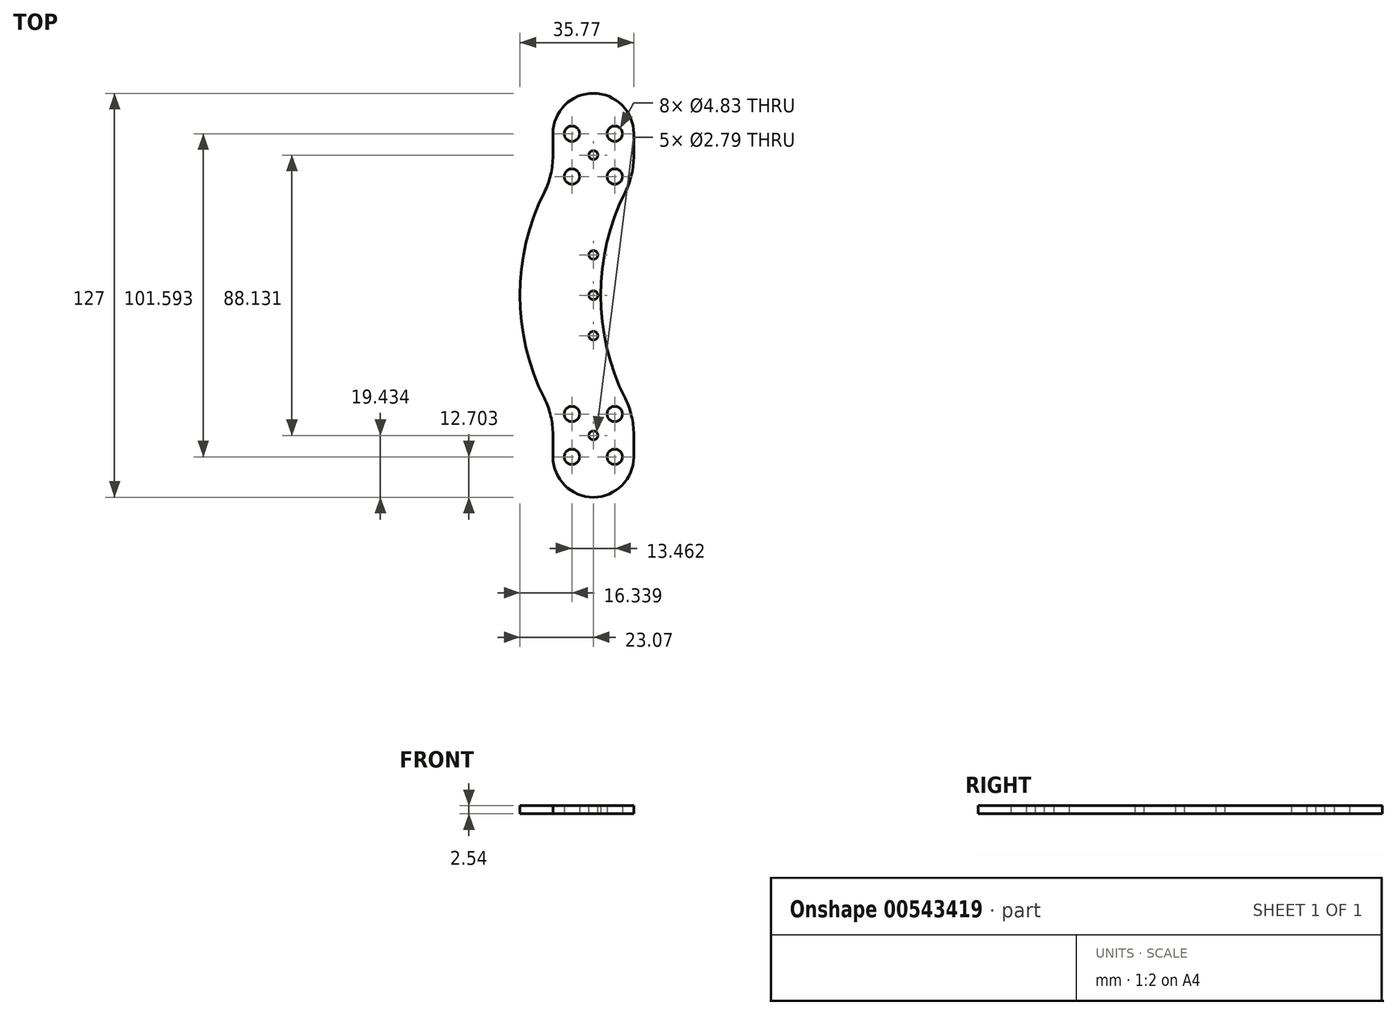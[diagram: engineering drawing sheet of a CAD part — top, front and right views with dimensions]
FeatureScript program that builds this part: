
annotation { "Feature Type Name" : "Feature", "Feature Type Description" : "" }
export const myFeature = defineFeature(function(context is Context, id is Id, definition is map)
    precondition{}
    {
        {
            var Q0;
            Q0=qCreatedBy(makeId("Top.planeOp"),FACE);
            var sketch = newSketch(context, id + "F0", { "sketchPlane" : qUnion([Q0])});
            skLineSegment(sketch, "E0.left", {"start": v(12.7, 50.8) * mm, "end": v(12.7, 37.33) * mm});
            skLineSegment(sketch, "E0.right", {"start": v(-12.7, 50.8) * mm, "end": v(-12.7, -50.8) * mm});
            skPoint(sketch, "E0.middle", {"position": v(0, 0) * mm});
            skLineSegment(sketch, "E1.bottom", {"start": v(6.73, -50.8) * mm, "end": v(-6.73, -50.8) * mm});
            skLineSegment(sketch, "E1.top", {"start": v(6.73, -37.33) * mm, "end": v(-6.73, -37.33) * mm});
            skLineSegment(sketch, "E1.left", {"start": v(6.73, -50.8) * mm, "end": v(6.73, -37.33) * mm});
            skLineSegment(sketch, "E1.right", {"start": v(-6.73, -50.8) * mm, "end": v(-6.73, -37.33) * mm});
            skPoint(sketch, "E1.middle", {"position": v(0, -44.07) * mm});
            skCircle(sketch, "E2", {"center": v(-6.73, -37.33) * mm, "radius": 2.41 * mm});
            skCircle(sketch, "E3", {"center": v(6.73, -37.33) * mm, "radius": 2.41 * mm});
            skCircle(sketch, "E4", {"center": v(6.73, -50.8) * mm, "radius": 2.41 * mm});
            skCircle(sketch, "E5", {"center": v(-6.73, -50.8) * mm, "radius": 2.41 * mm});
            skArc(sketch, "E6", {"start": v(-12.7, -50.8) * mm, "mid": v(0, -63.5) * mm, "end": v(12.7, -50.8) * mm});
            skArc(sketch, "E7", {"start": v(12.7, 50.8) * mm, "mid": v(0, 63.5) * mm, "end": v(-12.7, 50.8) * mm});
            skLineSegment(sketch, "E8", {"start": v(-8.67, 0) * mm, "end": v(8.23, 0) * mm});
            skCircle(sketch, "E9.MirrorC", {"center": v(-6.73, 37.33) * mm, "radius": 2.41 * mm});
            skCircle(sketch, "E10.MirrorC", {"center": v(6.73, 37.33) * mm, "radius": 2.41 * mm});
            skCircle(sketch, "E11.MirrorC", {"center": v(-6.73, 50.8) * mm, "radius": 2.41 * mm});
            skCircle(sketch, "E12.MirrorC", {"center": v(6.73, 50.8) * mm, "radius": 2.41 * mm});
            skLineSegment(sketch, "E13", {"start": v(12.7, 37.33) * mm, "end": v(-12.7, 37.33) * mm});
            skLineSegment(sketch, "E14", {"start": v(12.7, -37.33) * mm, "end": v(-12.7, -37.33) * mm});
            skArc(sketch, "E15", {"start": v(-12.7, 37.33) * mm, "mid": v(-23.07, 0) * mm, "end": v(-12.7, -37.33) * mm});
            skArc(sketch, "E16", {"start": v(12.7, 37.33) * mm, "mid": v(2.33, 0) * mm, "end": v(12.7, -37.33) * mm});
            skLineSegment(sketch, "E17.trimOffspring", {"start": v(12.7, -37.33) * mm, "end": v(12.7, -50.8) * mm});
            skSolve(sketch);
        }
        {
            var Q0;
            Q0=qSketchRegion(id+"F0",true);
            var Q1;
            {var subQ5=sQuery(id+"F0.wireOp",EDGE,"E4");var subQ10=sQuery(id+"F0.wireOp",EDGE,"E1.bottom");var subQ15=makeQuery(id+"F0.imprint","INTERSECT",VERTEX,{"derivedFrom":[subQ10,subQ5]});Q1=makeQuery(id+"F0.imprint","IMPRINT",FACE,{"disambiguationData":[TD([[makeQuery(id+"F0.imprint","IMPRINT",EDGE,{"disambiguationData":[TD([[subQ15,-1.0]])],"derivedFrom":subQ10}),-1.0]])]});}
            extrude(context, id + "F1", {"entities" : qUnion([Q0, Q1]), "depth" : 2.54 * mm, "offsetDistance" : 25.4 * mm});
        }
        {
            var Q0;
            Q0=makeQuery(id+"F1.opExtrude","CAP_FACE",FACE,{"disambiguationData":[OSD([sQuery(id+"F0.wireOp",EDGE,"E0.left"),sQuery(id+"F0.wireOp",EDGE,"E0.right"),sQuery(id+"F0.wireOp",EDGE,"E2"),sQuery(id+"F0.wireOp",EDGE,"E3"),sQuery(id+"F0.wireOp",EDGE,"E4"),sQuery(id+"F0.wireOp",EDGE,"E5"),sQuery(id+"F0.wireOp",EDGE,"E6"),sQuery(id+"F0.wireOp",EDGE,"E7")])],"isStart":false});
            var sketch = newSketch(context, id + "F2", { "sketchPlane" : qUnion([Q0])});
            skCircle(sketch, "E18", {"center": v(0, 0) * mm, "radius": 1.4 * mm});
            skLineSegment(sketch, "E19", {"start": v(-6.73, 50.8) * mm, "end": v(6.73, 37.33) * mm});
            skLineSegment(sketch, "E20", {"start": v(6.73, 50.8) * mm, "end": v(-6.73, 37.33) * mm});
            skCircle(sketch, "E21", {"center": v(0, 44.07) * mm, "radius": 1.4 * mm});
            skCircle(sketch, "E22.MirrorC", {"center": v(0, -44.07) * mm, "radius": 1.4 * mm});
            skLineSegment(sketch, "E23", {"start": v(0, 13.87) * mm, "end": v(0, -13.8) * mm});
            skCircle(sketch, "E24", {"center": v(0, 12.69) * mm, "radius": 1.4 * mm});
            skCircle(sketch, "E25", {"center": v(0, -12.71) * mm, "radius": 1.4 * mm});
            skPoint(sketch, "E26", {"position": v(0, -0.01) * mm});
            skSolve(sketch);
        }
        {
            var Q0;
            Q0=qSketchRegion(id+"F2",true);
            extrude(context, id + "F3", {"entities" : qUnion([Q0]), "operationType" : NewBodyOperationType.REMOVE, "endBound" : BoundingType.THROUGH_ALL, "oppositeDirection" : true, "depth" : 6.35 * mm, "offsetDistance" : 25.4 * mm});
        }
        {
            var Q0;
            Q0=makeQuery(id+"F1.opExtrude","SWEPT_EDGE",EDGE,{"disambiguationData":[OSD([sQuery(id+"F0.wireOp",EDGE,"E0.left"),sQuery(id+"F0.wireOp",EDGE,"E13"),sQuery(id+"F0.wireOp",EDGE,"E16")])]});
            var Q1;
            Q1=makeQuery(id+"F1.opExtrude","SWEPT_EDGE",EDGE,{"disambiguationData":[OSD([sQuery(id+"F0.wireOp",EDGE,"E14"),sQuery(id+"F0.wireOp",EDGE,"E16"),sQuery(id+"F0.wireOp",EDGE,"E17.trimOffspring")])]});
            var Q2;
            Q2=makeQuery(id+"F1.opExtrude","SWEPT_EDGE",EDGE,{"disambiguationData":[OSD([sQuery(id+"F0.wireOp",EDGE,"E0.right"),sQuery(id+"F0.wireOp",EDGE,"E13"),sQuery(id+"F0.wireOp",EDGE,"E15")])]});
            var Q3;
            Q3=makeQuery(id+"F1.opExtrude","SWEPT_EDGE",EDGE,{"disambiguationData":[OSD([sQuery(id+"F0.wireOp",EDGE,"E0.right"),sQuery(id+"F0.wireOp",EDGE,"E14"),sQuery(id+"F0.wireOp",EDGE,"E15")])]});
            fillet(context, id + "F4", {"entities" : qUnion([Q0, Q1, Q2, Q3]), "radius" : 25.4 * mm, "tangentPropagation" : true, "allowEdgeOverflow" : false});
        }
    });
